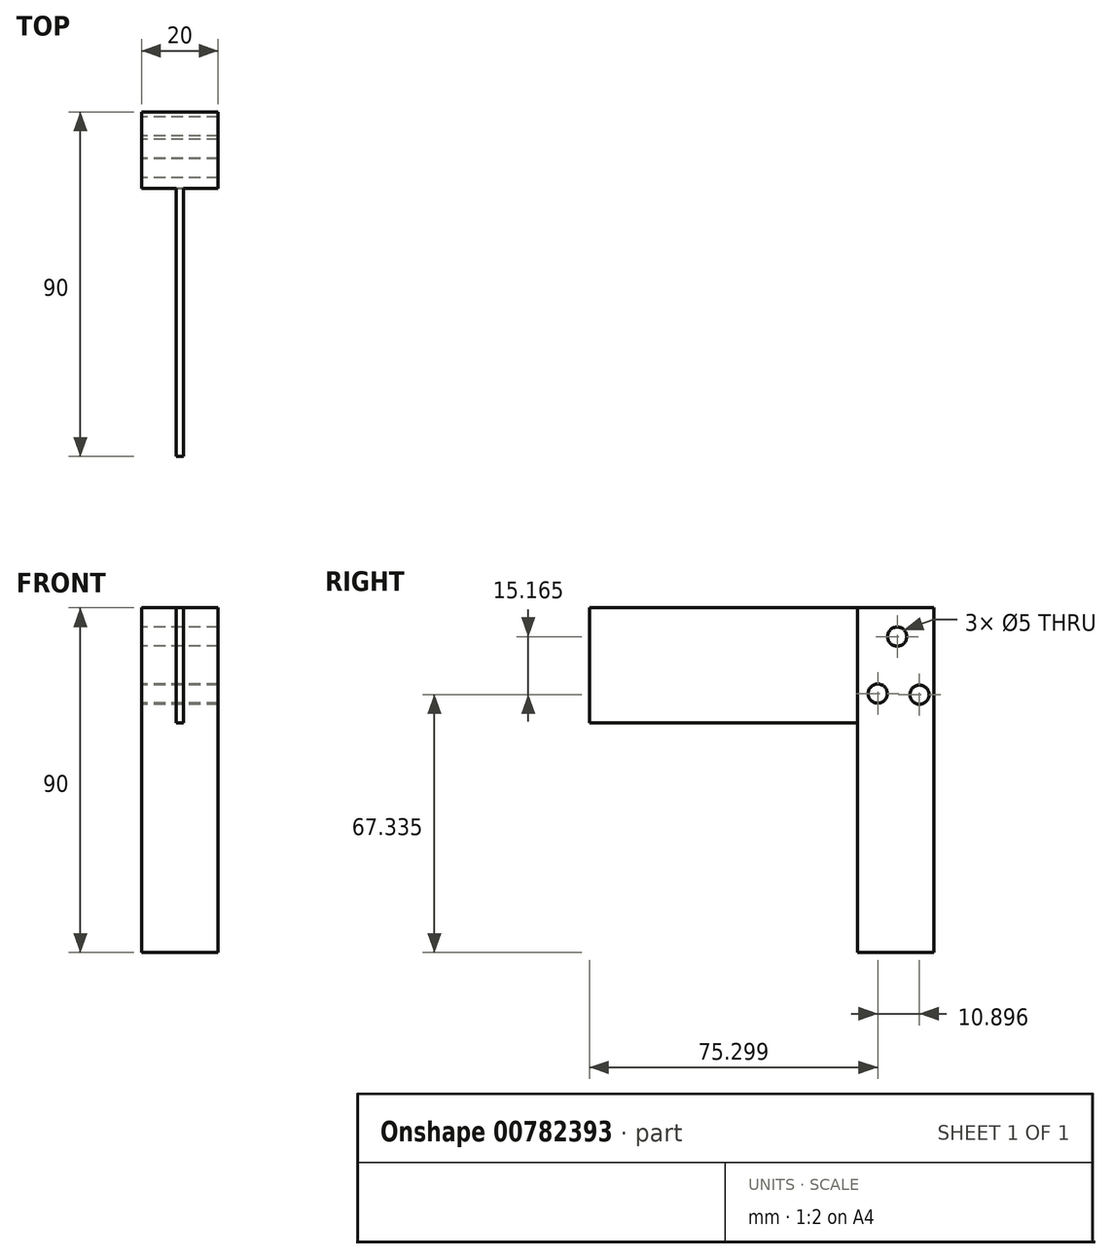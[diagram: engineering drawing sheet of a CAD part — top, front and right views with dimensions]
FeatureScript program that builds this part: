
annotation { "Feature Type Name" : "Feature", "Feature Type Description" : "" }
export const myFeature = defineFeature(function(context is Context, id is Id, definition is map)
    precondition{}
    {
        {
            var Q0;
            Q0=qCreatedBy(makeId("Front.planeOp"),FACE);
            var sketch = newSketch(context, id + "F0", { "sketchPlane" : qUnion([Q0])});
            skLineSegment(sketch, "E0.bottom", {"start": v(0, 0) * mm, "end": v(20, 0) * mm});
            skLineSegment(sketch, "E0.top", {"start": v(0, 90) * mm, "end": v(20, 90) * mm});
            skLineSegment(sketch, "E0.left", {"start": v(0, 0) * mm, "end": v(0, 90) * mm});
            skLineSegment(sketch, "E0.right", {"start": v(20, 0) * mm, "end": v(20, 90) * mm});
            skLineSegment(sketch, "E1.bottom", {"start": v(11, 90) * mm, "end": v(9, 90) * mm});
            skLineSegment(sketch, "E1.top", {"start": v(11, 60) * mm, "end": v(9, 60) * mm});
            skLineSegment(sketch, "E1.left", {"start": v(11, 90) * mm, "end": v(11, 60) * mm});
            skLineSegment(sketch, "E1.right", {"start": v(9, 90) * mm, "end": v(9, 60) * mm});
            skSolve(sketch);
        }
        {
            var Q0;
            Q0=makeQuery(id+"F0.imprint","IMPRINT",FACE,{"disambiguationData":[TD([[makeQuery(id+"F0.imprint","IMPRINT",EDGE,{"derivedFrom":sQuery(id+"F0.wireOp",EDGE,"E0.bottom")}),1.0]])]});
            extrude(context, id + "F1", {"entities" : qUnion([Q0]), "depth" : 20 * mm, "offsetDistance" : 25 * mm});
        }
        {
            var Q0;
            Q0=makeQuery(id+"F1.opExtrude","CAP_FACE",FACE,{"disambiguationData":[OSD([sQuery(id+"F0.wireOp",EDGE,"E0.bottom"),sQuery(id+"F0.wireOp",EDGE,"E0.top"),sQuery(id+"F0.wireOp",EDGE,"E0.left"),sQuery(id+"F0.wireOp",EDGE,"E0.right"),sQuery(id+"F0.wireOp",EDGE,"E1.top"),sQuery(id+"F0.wireOp",EDGE,"E1.left"),sQuery(id+"F0.wireOp",EDGE,"E1.right")])],"isStart":true});
            var sketch = newSketch(context, id + "F2", { "sketchPlane" : qUnion([Q0])});
            skLineSegment(sketch, "E2.bottom", {"start": v(-9, 60) * mm, "end": v(-11, 60) * mm});
            skLineSegment(sketch, "E2.top", {"start": v(-9, 90) * mm, "end": v(-11, 90) * mm});
            skLineSegment(sketch, "E2.left", {"start": v(-9, 60) * mm, "end": v(-9, 90) * mm});
            skLineSegment(sketch, "E2.right", {"start": v(-11, 60) * mm, "end": v(-11, 90) * mm});
            skSolve(sketch);
        }
        {
            var Q0;
            Q0=makeQuery(id+"F2.imprint","IMPRINT",FACE,{"disambiguationData":[TD([[makeQuery(id+"F2.imprint","IMPRINT",EDGE,{"derivedFrom":sQuery(id+"F2.wireOp",EDGE,"E2.bottom")}),1.0]])]});
            extrude(context, id + "F3", {"entities" : qUnion([Q0]), "operationType" : NewBodyOperationType.ADD, "oppositeDirection" : true, "depth" : 90 * mm, "offsetDistance" : 25 * mm});
        }
        {
            var Q0;
            Q0=makeQuery(id+"F1.opExtrude","SWEPT_FACE",FACE,{"disambiguationData":[OSD([sQuery(id+"F0.wireOp",EDGE,"E0.left")])]});
            var sketch = newSketch(context, id + "F4", { "sketchPlane" : qUnion([Q0])});
            skCircle(sketch, "E3", {"center": v(9.64, 82.5) * mm, "radius": 2.5 * mm});
            skCircle(sketch, "E4", {"center": v(3.8, 67.34) * mm, "radius": 2.5 * mm});
            skCircle(sketch, "E5", {"center": v(14.7, 67.62) * mm, "radius": 2.5 * mm});
            skSolve(sketch);
        }
        {
            var Q0;
            Q0=makeQuery(id+"F4.imprint","IMPRINT",FACE,{"disambiguationData":[TD([[makeQuery(id+"F4.imprint","IMPRINT",EDGE,{"derivedFrom":sQuery(id+"F4.wireOp",EDGE,"E3")}),1.0]])]});
            var Q1;
            Q1=makeQuery(id+"F4.imprint","IMPRINT",FACE,{"disambiguationData":[TD([[makeQuery(id+"F4.imprint","IMPRINT",EDGE,{"derivedFrom":sQuery(id+"F4.wireOp",EDGE,"E4")}),1.0]])]});
            var Q2;
            Q2=makeQuery(id+"F4.imprint","IMPRINT",FACE,{"disambiguationData":[TD([[makeQuery(id+"F4.imprint","IMPRINT",EDGE,{"derivedFrom":sQuery(id+"F4.wireOp",EDGE,"E5")}),1.0]])]});
            extrude(context, id + "F5", {"entities" : qUnion([Q0, Q1, Q2]), "operationType" : NewBodyOperationType.REMOVE, "oppositeDirection" : true, "depth" : 25 * mm, "offsetDistance" : 25 * mm});
        }
    });
